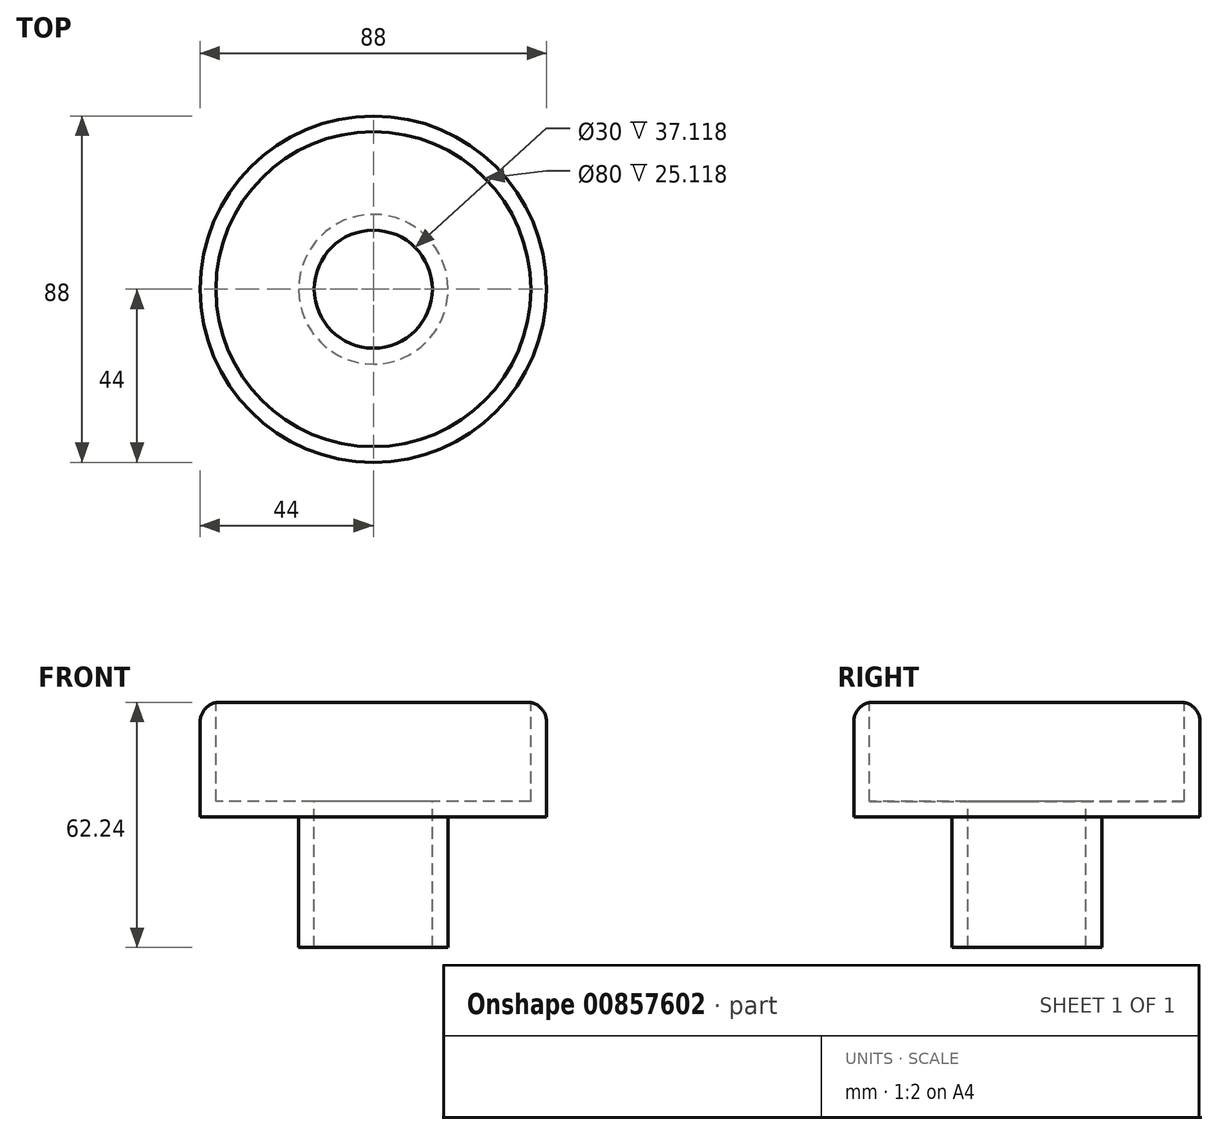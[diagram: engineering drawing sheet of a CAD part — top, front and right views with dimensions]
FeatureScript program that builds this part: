
annotation { "Feature Type Name" : "Feature", "Feature Type Description" : "" }
export const myFeature = defineFeature(function(context is Context, id is Id, definition is map)
    precondition{}
    {
        {
            var Q0;
            Q0=qCreatedBy(makeId("Front.planeOp"),FACE);
            var sketch = newSketch(context, id + "F0", { "sketchPlane" : qUnion([Q0])});
            skLineSegment(sketch, "E0", {"start": v(-44, 29.12) * mm, "end": v(-44, 0) * mm});
            skLineSegment(sketch, "E1", {"start": v(-44, 0) * mm, "end": v(-19, 0) * mm});
            skLineSegment(sketch, "E2", {"start": v(-19, -33.12) * mm, "end": v(-15, -33.12) * mm});
            skLineSegment(sketch, "E3", {"start": v(-15, -33.12) * mm, "end": v(-15, 4) * mm});
            skLineSegment(sketch, "E4", {"start": v(-15, 4) * mm, "end": v(-40, 4) * mm});
            skLineSegment(sketch, "E5", {"start": v(-40, 4) * mm, "end": v(-40, 29.12) * mm});
            skLineSegment(sketch, "E6", {"start": v(-40, 29.12) * mm, "end": v(-44, 29.12) * mm});
            skLineSegment(sketch, "E7", {"start": v(-19, 0) * mm, "end": v(-19, -33.12) * mm});
            skLineSegment(sketch, "E8", {"start": v(0, 65.6) * mm, "end": v(0, -67.43) * mm, "construction": true});
            skSolve(sketch);
        }
        {
            var Q0;
            Q0=makeQuery(id+"F0.imprint","IMPRINT",FACE,{"disambiguationData":[TD([[makeQuery(id+"F0.imprint","IMPRINT",EDGE,{"derivedFrom":sQuery(id+"F0.wireOp",EDGE,"E0")}),1.0]])]});
            var Q1;
            Q1=sQuery(id+"F0.wireOp",EDGE,"E8");
            revolve(context, id + "F1", {"surfaceOperationType" : NewSurfaceOperationType.NEW, "entities" : qUnion([Q0]), "axis" : qUnion([Q1]), "revolveType" : RevolveType.FULL});
        }
        {
            var Q0;
            Q0=makeQuery(id+"F1.opRevolve","SWEPT_EDGE",EDGE,{"disambiguationData":[OSD([sQuery(id+"F0.wireOp",EDGE,"E0"),sQuery(id+"F0.wireOp",EDGE,"E6")])]});
            fillet(context, id + "F2", {"entities" : qUnion([Q0]), "radius" : 5 * mm, "tangentPropagation" : true, "allowEdgeOverflow" : false});
        }
    });
